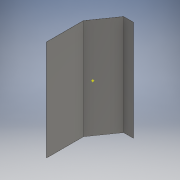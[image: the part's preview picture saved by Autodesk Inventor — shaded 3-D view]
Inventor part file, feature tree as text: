
AUTODESK INVENTOR PART (.ipt)
format: ipt  version: 2018 (Build 220112000, 112)  size: 135,680 bytes
history: native  units: mm
features: sheet_metal_op x3, other x2, sketch x1
ambient origin geometry x8: Origin, YZ Plane, XZ Plane, XY Plane, X Axis, Y Axis, Z Axis, Center Point
bodies: Solid1 (feature_tree)
feature tree (6):
  sheet_metal_op  "Contour Flange1"
  other  "Work Point1"
  sketch  "Sketch1"  dims[d0=440.0mm d1=345.0mm d2=25.307274mm d3=117.0mm d4=1.6mm d5=1.6mm d6=0.8mm d7=3.2mm d8=1.6mm d9=1200.0mm d10=1.6mm d11=1.6mm d12=6.4mm d13=1.6mm d14=1.6mm]
  other  "Plate1"
  sheet_metal_op  "Bend1"
  sheet_metal_op  "Corner1"
